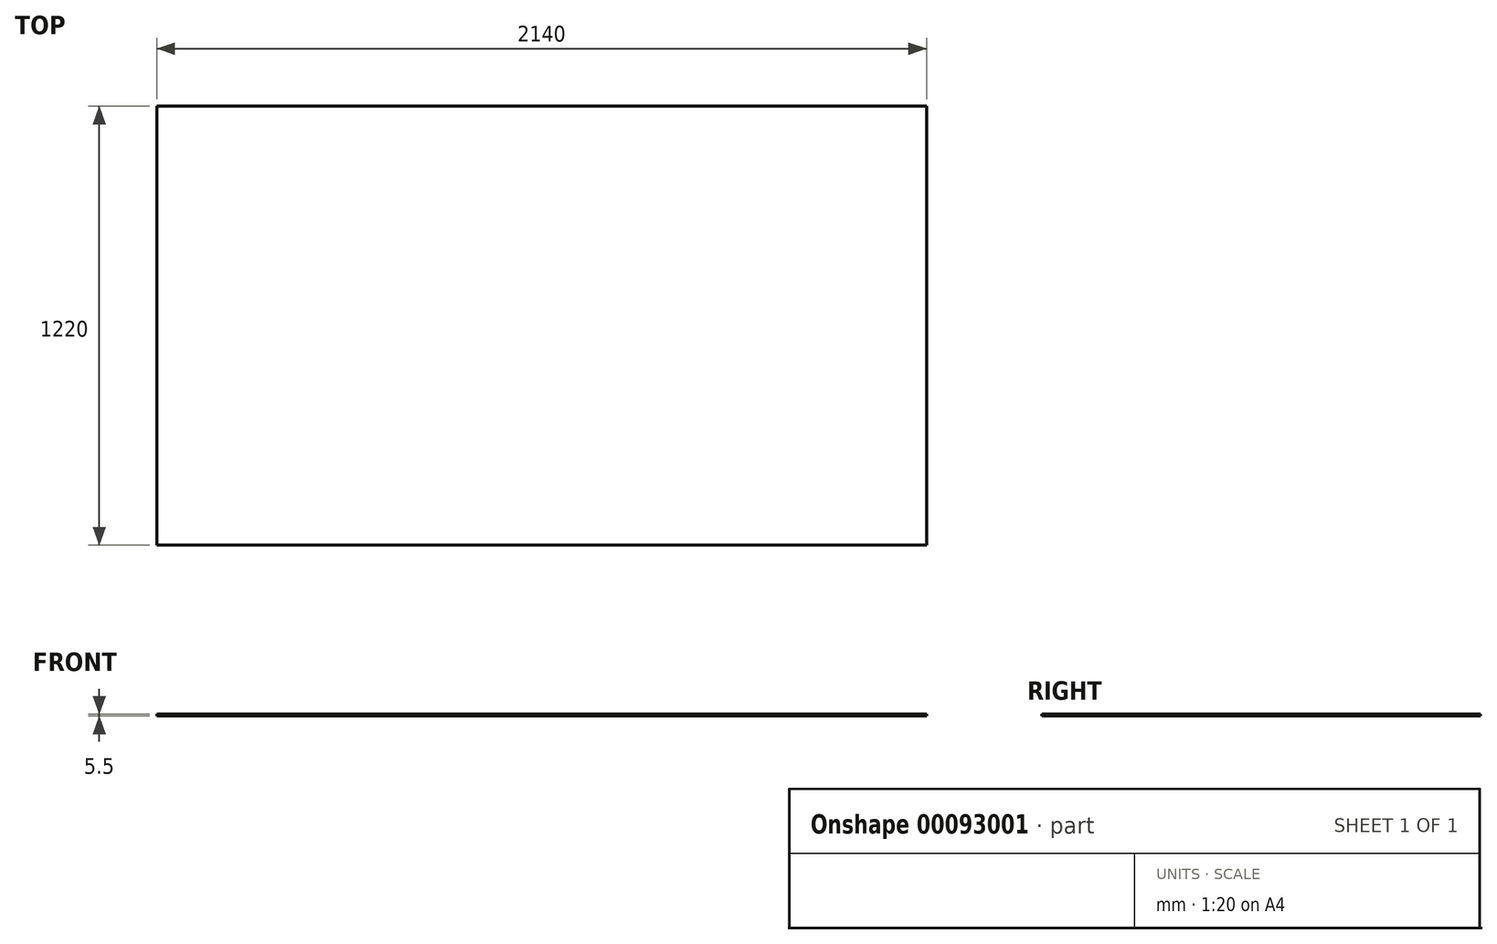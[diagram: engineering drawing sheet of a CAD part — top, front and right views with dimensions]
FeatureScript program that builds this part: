
annotation { "Feature Type Name" : "Feature", "Feature Type Description" : "" }
export const myFeature = defineFeature(function(context is Context, id is Id, definition is map)
    precondition{}
    {
        {
            var Q0;
            Q0=qCreatedBy(makeId("Top.planeOp"),FACE);
            var sketch = newSketch(context, id + "F0", { "sketchPlane" : qUnion([Q0])});
            skLineSegment(sketch, "E0.bottom", {"start": v(0, 0) * mm, "end": v(2140, 0) * mm});
            skLineSegment(sketch, "E0.top", {"start": v(0, 1220) * mm, "end": v(2140, 1220) * mm});
            skLineSegment(sketch, "E0.left", {"start": v(0, 0) * mm, "end": v(0, 1220) * mm});
            skLineSegment(sketch, "E0.right", {"start": v(2140, 0) * mm, "end": v(2140, 1220) * mm});
            skSolve(sketch);
        }
        {
            var Q0;
            Q0=makeQuery(id+"F0.imprint","IMPRINT",FACE,{"disambiguationData":[TD([[makeQuery(id+"F0.imprint","IMPRINT",EDGE,{"derivedFrom":sQuery(id+"F0.wireOp",EDGE,"E0.bottom")}),1.0]])]});
            extrude(context, id + "F1", {"entities" : qUnion([Q0]), "depth" : 5.5 * mm});
        }
    });
